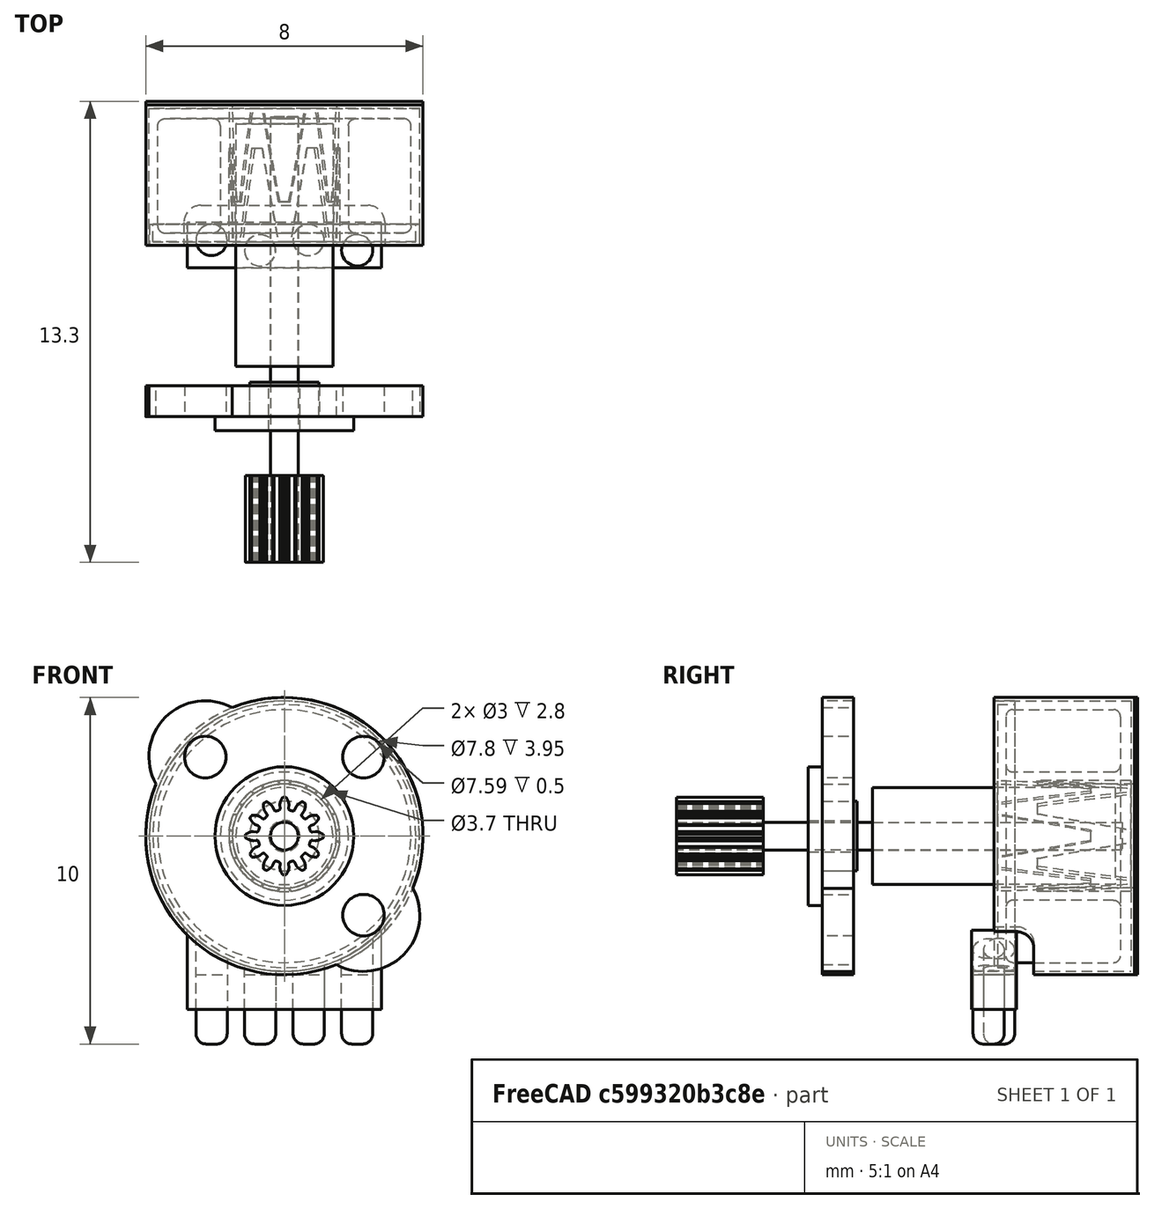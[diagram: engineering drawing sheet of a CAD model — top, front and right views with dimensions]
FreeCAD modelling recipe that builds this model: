
FCSTD DOCUMENT  (FreeCAD 1.0R39109 (Git))
Label: StepperMotor_8mm_i500212644_v4
License: All rights reserved
LicenseURL: https://en.wikipedia.org/wiki/All_rights_reserved
objects: PartDesign::Body×14, PartDesign::SubShapeBinder×13, Sketcher::SketchObject×7, PartDesign::Revolution×6, PartDesign::Plane×5, PartDesign::Pad×5, PartDesign::Pocket×5, PartDesign::FeatureBase×3, PartDesign::PolarPattern×2, PartDesign::Draft×2, App::VarSet×1, Part::Part2DObjectPython×1, PartDesign::Fillet×1, PartDesign::ShapeBinder×1, App::Part×1, App::Link×1, App::FeaturePython×1, Assembly::JointGroup×1, Assembly::AssemblyObject×1
note: 115 computed .brp shape members not serialized (recipe doc carries the construction recipe); baked Part::Feature solids carry a one-line shape summary decoded from their .brp

FEATURE [App::VarSet] VarSet
  Base_CanBodyInnerDiameter = 3
  Base_CanFingerMinorCircumference = 0.25
  Base_FingerClearanceAngle = 13.369
  BodyDiameter = 8
  BushingCollarLength = 1.4
  BushingCollarRadius = 1
  BushingFlangeRadius = 2
  BushingFlangeThickness = 0.4
  BushingMountingPlateClearance = 0.01
  BushingShaftClearance = 0.05
  CanBodyThickness = 0.1
  CanFingerLength = 1.25
  CoilBobbinDepth = 3.5
  CoilBobbinInternalRadius = 1.75
  CoilBobbinOuterRadius = 3.65
  CoilBobbinThickness = 0.1
  ConnectorBodyForwardClearance = 0.5
  ConnectorBodyHeight = 1
  ConnectorBodyLateralClearance = 0.1
  ConnectorBodyThickness = 1.3
  ConnectorBodyWidth = 5.6
  EndCapThickness = 0.1
  FingerClearance = 0.35
  FingerGusset = 0.5
  FingerRootAngle = 46.631
  FingerTeethAngle = 8
  GearHeadDiameter = 2.3
  GearHeadLength = 2.5
  MagnetCanClearance = 0.1
  MagnetLength = 7
  MagnetRadius = 1.4
  MountingHoleDiameter = 1.2
  MountingHolePitch = 6.4519
  MountingPlateThickness = 0.9
  NumFingers = 6
  PinDiameter = 0.9
  PinLength = 1
  PinOffset = 0.15
  PinPitch = 1.4
  PolePlateCanClearance = 0.005
  ShaftEndClearance = 0.45
  ShaftLength = 12.85
  ShaftThickness = 0.8
  TotalLength = 13.3
  expr: Base_CanFingerMinorCircumference = Base_CanBodyInnerDiameter / 2 - CanFingerLength
  expr: Base_FingerClearanceAngle = FingerClearance / (Base_CanBodyInnerDiameter * pi) * 360
  expr: FingerRootAngle = (Base_CanBodyInnerDiameter * pi / NumFingers - FingerClearance) / (Base_CanBodyInnerDiameter * pi) * 360
FEATURE [Sketcher::SketchObject] Sketch  label="MasterSketchFront"
  ArcFitTolerance = 1e-06
  AttachmentSupport = -> [XZ_Plane001]
  FullyConstrained = true
  MakeInternals = false
  MapMode = 5
  Placement = pos=(0,0,0) rot=(1,0,0;1.5708rad)
  expr: .Constraints.ConnectorBodyHeight = VarSet.ConnectorBodyHeight
  expr: Constraints[1] = VarSet.BodyDiameter
  expr: Constraints[27] = VarSet.PinPitch
  expr: Constraints[28] = VarSet.PinLength
  expr: Constraints[30] = VarSet.CanBodyThickness
  expr: Constraints[37] = VarSet.Base_CanBodyInnerDiameter
  expr: Constraints[38] = VarSet.CanFingerLength
  expr: Constraints[41] = VarSet.Base_CanBodyInnerDiameter / 2 - VarSet.CanFingerLength
  expr: Constraints[46] = VarSet.Base_FingerClearanceAngle
  expr: Constraints[47] = VarSet.FingerRootAngle
  expr: Constraints[49] = VarSet.CanBodyThickness * 2 + VarSet.Base_CanBodyInnerDiameter
  expr: Constraints[8] = VarSet.ConnectorBodyWidth
  sketch-geometry (22):
    g0: Circle CenterX=-1e-16 CenterY=0 CenterZ=0 NormalX=0 NormalY=0 NormalZ=1 AngleXU=0 Radius=4
    g1: LineSegment StartX=-2.8 StartY=-2.85657 StartZ=0 EndX=-2.8 EndY=-5 EndZ=0
    g2: LineSegment StartX=-2.8 StartY=-5 StartZ=0 EndX=2.8 EndY=-5 EndZ=0
    g3: LineSegment StartX=2.8 StartY=-5 StartZ=0 EndX=2.8 EndY=-2.85657 EndZ=0
    g4: LineSegment StartX=-2.1 StartY=-5 StartZ=0 EndX=-2.1 EndY=-6 EndZ=0
    g5: LineSegment StartX=-0.7 StartY=-5 StartZ=0 EndX=-0.7 EndY=-6 EndZ=0
    g6: LineSegment StartX=0.7 StartY=-5 StartZ=0 EndX=0.7 EndY=-6 EndZ=0
    g7: LineSegment StartX=2.1 StartY=-5 StartZ=0 EndX=2.1 EndY=-6 EndZ=0
    g8: LineSegment [constr] StartX=-2.1 StartY=-5 StartZ=0 EndX=-0.7 EndY=-5 EndZ=0
    g9: LineSegment [constr] StartX=-0.7 StartY=-5 StartZ=0 EndX=0.7 EndY=-5 EndZ=0
    g10: Circle CenterX=-1e-16 CenterY=0 CenterZ=0 NormalX=0 NormalY=0 NormalZ=1 AngleXU=0 Radius=3.9
    g11: Circle CenterX=-1e-16 CenterY=0 CenterZ=0 NormalX=0 NormalY=0 NormalZ=1 AngleXU=0 Radius=1.5
    g12: ArcOfCircle CenterX=-1e-16 CenterY=0 CenterZ=0 NormalX=0 NormalY=0 NormalZ=1 AngleXU=0 Radius=0.25 StartAngle=1.16386 EndAngle=1.97773
    g13: LineSegment StartX=-0.0989485 StartY=0.229585 StartZ=0 EndX=-0.593691 EndY=1.37751 EndZ=0
    g14: LineSegment StartX=0.0989485 StartY=0.229585 StartZ=0 EndX=0.593691 EndY=1.37751 EndZ=0
    g15: LineSegment StartX=-0.896112 StartY=1.20291 StartZ=0 EndX=-2e-16 EndY=0 EndZ=0
    g16: LineSegment [constr] StartX=-0.593691 StartY=1.37751 StartZ=0 EndX=-1e-16 EndY=0 EndZ=0
    g17: Circle CenterX=-1e-16 CenterY=0 CenterZ=0 NormalX=0 NormalY=0 NormalZ=1 AngleXU=0 Radius=1.6
    g18: LineSegment StartX=-0.896112 StartY=1.20291 StartZ=0 EndX=-0.955853 EndY=1.2831 EndZ=0
    g19: LineSegment StartX=-0.593691 StartY=1.37751 StartZ=0 EndX=-0.63327 EndY=1.46934 EndZ=0
    g20: LineSegment StartX=0.593691 StartY=1.37751 StartZ=0 EndX=0.63327 EndY=1.46934 EndZ=0
    g21: GeomPoint X=0 Y=-5 Z=0
  constraints (60):
    c: Coincident(g0,g-1)
    c: Diameter(g0) = 8
    c: Coincident(g1,g2)
    c: Coincident(g2,g3)
    c: Vertical(g1)
    c: Vertical(g3)
    c: PointOnObject(g1,g0)
    c: PointOnObject(g3,g0)
    c: DistanceX(g2,g2) = 5.6
    c: Symmetric(g2,g1,g-2)
    c: Distance(g0,g2) = 1  'ConnectorBodyHeight'
    c: PointOnObject(g4,g2)
    c: Vertical(g4)
    c: PointOnObject(g5,g2)
    c: Vertical(g5)
    c: Vertical(g6)
    c: Vertical(g7)
    c: Equal(g7,g6)
    c: Equal(g6,g5)
    c: Equal(g5,g4)
    c: Symmetric(g7,g4,g-2)
    c: Symmetric(g5,g6,g-2)
    c: Coincident(g8,g4)
    c: Coincident(g8,g5)
    c: Coincident(g9,g5)
    c: Coincident(g9,g6)
    c: Equal(g8,g9)
    c: Distance(g5,g4) = 1.4
    c: DistanceY(g4,g4) = 1
    c: Coincident(g10,g0)
    c: Distance(g10,g0) = 0.1
    c: Coincident(g11,g0)
    c: Coincident(g12,g0)
    c: PointOnObject(g13,g11)
    c: PointOnObject(g14,g11)
    c: Horizontal(g14,g13)
    c: Horizontal(g14,g13)
    c: Diameter(g11) = 3
    c: Distance(g14,g14) = 1.25
    c: Coincident(g12,g13)
    c: Coincident(g12,g14)
    c: Radius(g12) = 0.25
    c: PointOnObject(g15,g11)
    c: Coincident(g15,g0)
    c: Coincident(g16,g13)
    c: Coincident(g16,g0)
    c: Angle(g13,g15) = 0.233333
    c: Angle(g14,g13) = 0.813864
    c: Coincident(g17,g0)
    c: Diameter(g17) = 3.2
    c: Coincident(g18,g15)
    c: PointOnObject(g18,g17)
    c: Coincident(g19,g13)
    c: PointOnObject(g19,g17)
    c: Perpendicular(g11,g19)
    c: Perpendicular(g11,g18)
    c: Coincident(g20,g14)
    c: PointOnObject(g20,g17)
    c: Perpendicular(g11,g20)
    c: Symmetric(g2,g2,g21)
FEATURE [Sketcher::SketchObject] Sketch001  label="MasterSketchRight"
  ArcFitTolerance = 1e-06
  AttachmentSupport = -> [YZ_Plane001]
  ExternalGeometry = -> [Sketch]
  FullyConstrained = false
  MakeInternals = false
  MapMode = 5
  Placement = pos=(0,0,0) rot=(0.57735,0.57735,0.57735;2.0944rad)
  expr: .Constraints.BushingFlangeRadius = VarSet.BushingFlangeRadius
  expr: .Constraints.BushingShaftClearance = VarSet.BushingShaftClearance
  expr: .Constraints.EndCapThickness = VarSet.EndCapThickness
  expr: .Constraints.ShaftThickness = VarSet.ShaftThickness
  expr: Constraints[116] = VarSet.PolePlateCanClearance
  expr: Constraints[161] = VarSet.CoilBobbinThickness
  expr: Constraints[162] = VarSet.CoilBobbinInternalRadius
  expr: Constraints[163] = VarSet.CoilBobbinDepth
  expr: Constraints[164] = VarSet.CoilBobbinOuterRadius
  expr: Constraints[194] = VarSet.Base_CanBodyInnerDiameter / 2
  expr: Constraints[195] = VarSet.CanFingerLength
  expr: Constraints[59] = VarSet.BushingCollarRadius
  expr: Constraints[60] = VarSet.BushingMountingPlateClearance
  expr: Constraints[61] = VarSet.BushingFlangeThickness
  expr: Constraints[63] = VarSet.BushingCollarLength
  expr: Constraints[65] = VarSet.GearHeadDiameter
  expr: Constraints[66] = VarSet.GearHeadLength
  expr: Constraints[67] = VarSet.MountingPlateThickness
  expr: Constraints[71] = VarSet.TotalLength
  expr: Constraints[72] = VarSet.ShaftLength
  expr: Constraints[92] = VarSet.MagnetRadius
  expr: Constraints[93] = VarSet.MagnetLength
  sketch-geometry (80):
    g0: LineSegment StartX=0 StartY=0 StartZ=0 EndX=3.7 EndY=0 EndZ=0
    g1: LineSegment StartX=0 StartY=0 StartZ=0 EndX=-9.15 EndY=0 EndZ=0
    g2: GeomPoint X=-6.65 Y=0 Z=0
    g3: GeomPoint X=-5.35 Y=0 Z=0
    g4: GeomPoint X=-4.05 Y=0 Z=0
    g5: GeomPoint X=-4.95 Y=0 Z=0
    g6: GeomPoint X=3.7 Y=0 Z=0
    g7: LineSegment StartX=-9.15 StartY=1.15 StartZ=0 EndX=-9.15 EndY=-1.15 EndZ=0
    g8: LineSegment StartX=-9.15 StartY=-1.15 StartZ=0 EndX=-6.65 EndY=-1.15 EndZ=0
    g9: LineSegment StartX=-6.65 StartY=-1.15 StartZ=0 EndX=-6.65 EndY=1.15 EndZ=0
    g10: LineSegment StartX=-6.65 StartY=1.15 StartZ=0 EndX=-9.15 EndY=1.15 EndZ=0
    g11: LineSegment StartX=-9.15 StartY=0.4 StartZ=0 EndX=-9.15 EndY=-0.4 EndZ=0
    g12: LineSegment StartX=-9.15 StartY=-0.4 StartZ=0 EndX=3.7 EndY=-0.4 EndZ=0
    g13: LineSegment StartX=3.7 StartY=-0.4 StartZ=0 EndX=3.7 EndY=0.4 EndZ=0
    g14: LineSegment StartX=3.7 StartY=0.4 StartZ=0 EndX=0 EndY=0.4 EndZ=0
    g15: LineSegment StartX=-5.35 StartY=2 StartZ=0 EndX=-5.35 EndY=0.45 EndZ=0
    g16: LineSegment StartX=-5.35 StartY=0.45 StartZ=0 EndX=-3.95 EndY=0.45 EndZ=0
    g17: LineSegment StartX=-3.95 StartY=0.45 StartZ=0 EndX=-3.95 EndY=1 EndZ=0
    g18: LineSegment StartX=-4.95 StartY=1 StartZ=0 EndX=-4.95 EndY=2 EndZ=0
    g19: LineSegment StartX=-4.95 StartY=2 StartZ=0 EndX=-5.35 EndY=2 EndZ=0
    g20: LineSegment StartX=-4.95 StartY=4 StartZ=0 EndX=-4.95 EndY=1.01 EndZ=0
    g21: LineSegment StartX=-4.95 StartY=1.01 StartZ=0 EndX=-4.05 EndY=1.01 EndZ=0
    g22: LineSegment StartX=-4.05 StartY=4 StartZ=0 EndX=-4.95 EndY=4 EndZ=0
    g23: LineSegment StartX=4.15 StartY=4 StartZ=0 EndX=4.15 EndY=0 EndZ=0
    g24: LineSegment StartX=4.05 StartY=0 StartZ=0 EndX=4.05 EndY=4 EndZ=0
    g25: LineSegment StartX=4.05 StartY=4 StartZ=0 EndX=4.15 EndY=4 EndZ=0
    g26: LineSegment StartX=-4.05 StartY=4 StartZ=0 EndX=9e-16 EndY=4 EndZ=0
    g27: LineSegment StartX=9e-16 StartY=4 StartZ=0 EndX=4.05 EndY=4 EndZ=0
    g28: LineSegment StartX=-4.95 StartY=1 StartZ=0 EndX=-3.95 EndY=1 EndZ=0
    g29: GeomPoint X=4.05 Y=0 Z=0
    g30: LineSegment StartX=-3.95 StartY=3.9 StartZ=0 EndX=-3.95 EndY=1.6 EndZ=0
    g31: LineSegment StartX=9e-16 StartY=3.9 StartZ=0 EndX=-3.95 EndY=3.9 EndZ=0
    g32: LineSegment StartX=-3.5 StartY=0.4 StartZ=0 EndX=3.5 EndY=0.4 EndZ=0
    g33: LineSegment StartX=3.5 StartY=0.4 StartZ=0 EndX=3.5 EndY=1.4 EndZ=0
    g34: LineSegment StartX=3.5 StartY=1.4 StartZ=0 EndX=-3.5 EndY=1.4 EndZ=0
    g35: LineSegment StartX=-3.5 StartY=1.4 StartZ=0 EndX=-3.5 EndY=0.4 EndZ=0
    g36: LineSegment [constr] StartX=9e-16 StartY=3.9 StartZ=0 EndX=9e-16 EndY=4 EndZ=0
    g37: LineSegment [constr] StartX=-3.95 StartY=3.9 StartZ=0 EndX=-4.05 EndY=3.9 EndZ=0
    g38: GeomPoint X=0 Y=1.4 Z=0
    g39: LineSegment StartX=-0.6 StartY=3.895 StartZ=0 EndX=9e-16 EndY=3.895 EndZ=0
    g40: LineSegment StartX=9e-16 StartY=3.895 StartZ=0 EndX=4e-16 EndY=1.5 EndZ=0
    g41: LineSegment StartX=-0.1 StartY=1.6 StartZ=0 EndX=-0.1 EndY=3.795 EndZ=0
    g42: LineSegment StartX=-0.1 StartY=3.795 StartZ=0 EndX=-0.6 EndY=3.795 EndZ=0
    g43: LineSegment StartX=-0.6 StartY=3.795 StartZ=0 EndX=-0.6 EndY=3.895 EndZ=0
    g44: LineSegment [constr] StartX=-0.1 StartY=3.795 StartZ=0 EndX=8e-16 EndY=3.795 EndZ=0
    g45: LineSegment StartX=-1.25 StartY=1.6 StartZ=0 EndX=-1.25 EndY=1.5 EndZ=0
    g46: LineSegment StartX=-3.95 StartY=1.6 StartZ=0 EndX=-1.25 EndY=1.6 EndZ=0
    g47: LineSegment StartX=-0.1 StartY=1.6 StartZ=0 EndX=-2.8 EndY=1.6 EndZ=0
    g48: LineSegment StartX=9e-16 StartY=3.895 StartZ=0 EndX=4e-16 EndY=1.5 EndZ=0
    g49: LineSegment StartX=-3.65 StartY=3.45 StartZ=0 EndX=-3.65 EndY=2.05 EndZ=0
    g50: LineSegment StartX=-3.45 StartY=1.85 StartZ=0 EndX=-0.55 EndY=1.85 EndZ=0
    g51: LineSegment StartX=-0.35 StartY=2.05 StartZ=0 EndX=-0.35 EndY=3.45 EndZ=0
    g52: LineSegment StartX=-0.55 StartY=3.65 StartZ=0 EndX=-3.45 EndY=3.65 EndZ=0
    g53: ArcOfCircle CenterX=-3.45 CenterY=3.45 CenterZ=0 NormalX=0 NormalY=0 NormalZ=1 AngleXU=0 Radius=0.2 StartAngle=1.5708 EndAngle=3.14159
    g54: ArcOfCircle CenterX=-3.45 CenterY=2.05 CenterZ=0 NormalX=0 NormalY=0 NormalZ=1 AngleXU=0 Radius=0.2 StartAngle=3.14159 EndAngle=4.71239
    g55: ArcOfCircle CenterX=-0.55 CenterY=2.05 CenterZ=0 NormalX=0 NormalY=0 NormalZ=1 AngleXU=0 Radius=0.2 StartAngle=4.71239 EndAngle=6.28319
    g56: ArcOfCircle CenterX=-0.55 CenterY=3.45 CenterZ=0 NormalX=0 NormalY=0 NormalZ=1 AngleXU=0 Radius=0.2 StartAngle=3e-16 EndAngle=1.5708
    g57: GeomPoint [constr] X=-3.65 Y=3.65 Z=0
    g58: GeomPoint [constr] X=-0.35 Y=1.85 Z=0
    g59: LineSegment StartX=-3.75 StartY=3.65 StartZ=0 EndX=-3.65 EndY=3.65 EndZ=0
    g60: LineSegment StartX=-3.65 StartY=3.65 StartZ=0 EndX=-3.65 EndY=1.85 EndZ=0
    g61: LineSegment StartX=-3.65 StartY=1.85 StartZ=0 EndX=-0.35 EndY=1.85 EndZ=0
    g62: LineSegment StartX=-0.35 StartY=1.85 StartZ=0 EndX=-0.35 EndY=3.65 EndZ=0
    g63: LineSegment StartX=-0.35 StartY=3.65 StartZ=0 EndX=-0.25 EndY=3.65 EndZ=0
    g64: LineSegment StartX=-0.25 StartY=3.65 StartZ=0 EndX=-0.25 EndY=1.75 EndZ=0
    g65: LineSegment StartX=-0.25 StartY=1.75 StartZ=0 EndX=-3.75 EndY=1.75 EndZ=0
    g66: LineSegment StartX=-3.75 StartY=1.75 StartZ=0 EndX=-3.75 EndY=3.65 EndZ=0
    g67: LineSegment [constr] StartX=-0.35 StartY=1.85 StartZ=0 EndX=-0.35 EndY=1.75 EndZ=0
    g68: LineSegment [constr] StartX=9e-16 StartY=3.9 StartZ=0 EndX=9e-16 EndY=4 EndZ=0
    g69: LineSegment StartX=9e-16 StartY=4 StartZ=0 EndX=9e-16 EndY=3.9 EndZ=0
    g70: LineSegment StartX=-4.05 StartY=1.01 StartZ=0 EndX=-4.05 EndY=1.5 EndZ=0
    g71: LineSegment StartX=-4.05 StartY=1.5 StartZ=0 EndX=-4.05 EndY=3.9 EndZ=0
    g72: LineSegment StartX=-4.05 StartY=3.9 StartZ=0 EndX=-4.05 EndY=4 EndZ=0
    g73: LineSegment StartX=-1.25 StartY=1.6 StartZ=0 EndX=-2.8 EndY=1.6 EndZ=0
    g74: LineSegment StartX=-4.05 StartY=1.5 StartZ=0 EndX=-1.25 EndY=1.5 EndZ=0
    g75: LineSegment StartX=-1.25 StartY=1.5 StartZ=0 EndX=-2.8 EndY=1.5 EndZ=0
    g76: LineSegment StartX=-2.8 StartY=1.6 StartZ=0 EndX=-2.8 EndY=1.5 EndZ=0
    g77: LineSegment StartX=-2.8 StartY=1.5 StartZ=0 EndX=4e-16 EndY=1.5 EndZ=0
    g78: LineSegment StartX=4.05 StartY=0 StartZ=0 EndX=4.15 EndY=0 EndZ=0
    g79: LineSegment StartX=-3.5 StartY=0.4 StartZ=0 EndX=-9.15 EndY=0.4 EndZ=0
  constraints (205):
    c: Coincident(g0,g-1)
    c: PointOnObject(g78,g-1)
    c: Coincident(g1,g0)
    c: PointOnObject(g1,g-1)
    c: PointOnObject(g2,g1)
    c: PointOnObject(g4,g1)
    c: PointOnObject(g5,g1)
    c: PointOnObject(g6,g0)
    c: Coincident(g7,g8)
    c: Coincident(g8,g9)
    c: Coincident(g9,g10)
    c: Coincident(g10,g7)
    c: Vertical(g7)
    c: Vertical(g9)
    c: Horizontal(g8)
    c: Symmetric(g7,g7,g1)
    c: Symmetric(g8,g9,g2)
    c: Coincident(g11,g12)
    c: Coincident(g12,g13)
    c: Coincident(g13,g14)
    c: Coincident(g79,g11)
    c: Vertical(g11)
    c: Vertical(g13)
    c: Horizontal(g12)
    c: Symmetric(g12,g13,g6)
    c: Vertical(g15)
    c: Coincident(g15,g16)
    c: Horizontal(g16)
    c: Coincident(g16,g17)
    c: Vertical(g18)
    c: Coincident(g18,g19)
    c: Coincident(g19,g15)
    c: Horizontal(g19)
    c: Vertical(g17)
    c: Vertical(g3,g15)
    c: Coincident(g20,g21)
    c: Coincident(g22,g20)
    c: Horizontal(g21)
    c: Horizontal(g22)
    c: Vertical(g20,g5)
    c: Vertical(g21,g4)
    c: Distance(g12,g14) = 0.8  'ShaftThickness'
    c: Distance(g15,g14) = 0.05  'BushingShaftClearance'
    c: DistanceY(g3,g15) = 2  'BushingFlangeRadius'
    c: Coincident(g24,g25)
    c: Coincident(g25,g23)
    c: Vertical(g23)
    c: Vertical(g24)
    c: Horizontal(g25)
    c: Distance(g23,g24) = 0.1  'EndCapThickness'
    c: Coincident(g26,g-3)
    c: Horizontal(g26)
    c: Coincident(g27,g26)
    c: Coincident(g27,g24)
    c: Symmetric(g24,g22,g26)
    c: DistanceX(g20,g23) = 9.1  'MeasuredBodyLength'
    c: Coincident(g28,g18)
    c: Coincident(g28,g17)
    c: Horizontal(g28)
    c: DistanceY(g4,g17) = 1
    c: Distance(g21,g28) = 0.01
    c: Distance(g19,g19) = 0.4
    c: Tangent(g18,g20)
    c: DistanceX(g15,g16) = 1.4
    c: Symmetric(g11,g11,g1)
    c: DistanceY(g7,g7) = 2.3
    c: DistanceX(g10,g10) = 2.5
    c: DistanceX(g22,g22) = 0.9
    c: PointOnObject(g3,g1)
    c: PointOnObject(g29,g78)
    c: PointOnObject(g29,g24)
    c: DistanceX(g1,g78) = 13.3
    c: DistanceX(g1,g6) = 12.85
    c: DistanceX(g13,g29) = 0.35  'ShafteendClearance'
    c: Coincident(g31,g30)
    c: Vertical(g30)
    c: Horizontal(g31)
    c: Coincident(g32,g33)
    c: Coincident(g33,g34)
    c: Coincident(g34,g35)
    c: Coincident(g35,g32)
    c: Horizontal(g32)
    c: Horizontal(g34)
    c: Vertical(g33)
    c: Vertical(g35)
    c: PointOnObject(g32,g79)
    c: Coincident(g36,g31)
    c: Coincident(g36,g26)
    c: Coincident(g37,g30)
    c: Horizontal(g37)
    c: Equal(g37,g36)
    c: Coincident(g31,g-4)
    c: Distance(g0,g34) = 1.4
    c: Distance(g33,g35) = 7
    c: Symmetric(g34,g34,g38)
    c: Vertical(g38,g0)
    c: PointOnObject(g39,g-4)
    c: Horizontal(g39)
    c: Coincident(g39,g40)
    c: PointOnObject(g40,g-4)
    c: Vertical(g41)
    c: Coincident(g41,g42)
    c: Horizontal(g42)
    c: Coincident(g42,g43)
    c: Coincident(g43,g39)
    c: Vertical(g43)
    c: Coincident(g44,g41)
    c: PointOnObject(g44,g40)
    c: Horizontal(g44)
    c: Equal(g44,g43)
    c: Vertical(g45)
    c: Coincident(g46,g30)
    c: Coincident(g46,g45)
    c: Horizontal(g46)
    c: Coincident(g47,g41)
    c: Horizontal(g47)
    c: Distance(g31,g39) = 0.005
    c: DistanceX(g42,g42) = 0.5  'PolePlateFlangeLength'
    c: Equal(g47,g46)
    c: Coincident(g48,g39)
    c: Coincident(g48,g40)
    c: Tangent(g49,g53) = -1.5708
    c: Tangent(g49,g54) = -1.5708
    c: Tangent(g50,g54) = -1.5708
    c: Tangent(g50,g55) = -1.5708
    c: Tangent(g51,g55) = -1.5708
    c: Tangent(g51,g56) = -1.5708
    c: Tangent(g52,g56) = -1.5708
    c: Tangent(g52,g53) = -1.5708
    c: Vertical(g49)
    c: Vertical(g51)
    c: Horizontal(g50)
    c: Horizontal(g52)
    c: Equal(g53,g54)
    c: Equal(g54,g55)
    c: Equal(g55,g56)
    c: PointOnObject(g57,g49)
    c: PointOnObject(g57,g52)
    c: PointOnObject(g58,g50)
    c: PointOnObject(g58,g51)
    c: Coincident(g59,g60)
    c: Coincident(g60,g61)
    c: Coincident(g61,g62)
    c: Coincident(g62,g63)
    c: Coincident(g63,g64)
    c: Vertical(g64)
    c: Coincident(g64,g65)
    c: Horizontal(g65)
    c: Coincident(g65,g66)
    c: Coincident(g66,g59)
    c: Vertical(g66)
    c: Equal(g59,g63)
    c: Tangent(g49,g60)
    c: Tangent(g51,g62)
    c: Tangent(g63,g59)
    c: Tangent(g59,g52)
    c: Tangent(g50,g61)
    c: Coincident(g67,g58)
    c: PointOnObject(g67,g65)
    c: Vertical(g67)
    c: Equal(g67,g63)
    c: Distance(g49,g66) = 0.1
    c: DistanceY(g0,g64) = 1.75
    c: DistanceX(g65,g64) = 3.5
    c: DistanceY(g0,g63) = 3.65
    c: Coincident(g68,g31)
    c: Coincident(g68,g26)
    c: Coincident(g69,g26)
    c: Coincident(g69,g31)
    c: Coincident(g70,g21)
    c: Vertical(g70)
    c: Coincident(g71,g37)
    c: Vertical(g71)
    c: Coincident(g72,g37)
    c: Coincident(g72,g22)
    c: Coincident(g26,g22)
    c: Coincident(g73,g45)
    c: Coincident(g73,g47)
    c: Horizontal(g73)
    c: Coincident(g74,g70)
    c: Coincident(g74,g45)
    c: Horizontal(g74)
    c: Coincident(g75,g45)
    c: Horizontal(g75)
    c: Coincident(g76,g47)
    c: Coincident(g76,g75)
    c: Coincident(g77,g75)
    c: Coincident(g77,g40)
    c: Horizontal(g77)
    c: Vertical(g76)
    c: Coincident(g71,g70)
    c: Vertical(g72)
    c: Equal(g45,g37)
    c: Equal(g44,g37)
    c: Distance(g40,g0) = 1.5
    c: DistanceX(g45,g40) = 1.25
    c: PointOnObject(g24,g78)
    c: Coincident(g78,g23)
    c: PointOnObject(g0,g13)
    c: PointOnObject(g78,g24)
    c: Distance(g41,g64) = 0.15  'BobbinOffset'
    c: Radius(g53) = 0.2  'CoilRoundness'
    c: Horizontal(g0)
    c: Horizontal(g78)
    c: PointOnObject(g14,g-4)
FEATURE [PartDesign::Plane] DatumPlane  label="GearHeadDatum"
  AttachmentSupport = -> [Sketch001,XZ_Plane001]
  Length = 10
  MapMode = 6
  Placement = pos=(0,-9.15,0) rot=(0.57735,-0.57735,0.57735;2.0944rad)
  ResizeMode = 1
  Width = 10
FEATURE [PartDesign::Plane] DatumPlane001  label="BushingFlangeDatum"
  AttachmentSupport = -> [Sketch001,XZ_Plane001]
  Length = 10
  MapMode = 6
  Placement = pos=(0,-5.35,0) rot=(0.57735,-0.57735,0.57735;2.0944rad)
  ResizeMode = 1
  Width = 10
FEATURE [PartDesign::Plane] DatumPlane002  label="MountingPlateDatum"
  AttachmentSupport = -> [Sketch001,XZ_Plane001]
  Length = 10
  MapMode = 6
  Placement = pos=(0,-4.95,0) rot=(0.57735,-0.57735,0.57735;2.0944rad)
  ResizeMode = 1
  Width = 10
FEATURE [PartDesign::Plane] DatumPlane003  label="EndCapDatum"
  AttachmentSupport = -> [Sketch001,XZ_Plane001]
  Length = 10
  MapMode = 6
  Placement = pos=(0,4.05,0) rot=(0.57735,-0.57735,0.57735;2.0944rad)
  ResizeMode = 1
  Width = 10
FEATURE [Sketcher::SketchObject] Sketch002
  ArcFitTolerance = 1e-06
  AttachmentSupport = -> [DatumPlane]
  FullyConstrained = true
  MakeInternals = false
  MapMode = 5
  Placement = pos=(0,-9.15,0) rot=(0.57735,-0.57735,0.57735;2.0944rad)
  expr: Constraints[1] = VarSet.ShaftThickness
  sketch-geometry (1):
    g0: Circle CenterX=0 CenterY=0 CenterZ=0 NormalX=0 NormalY=0 NormalZ=1 AngleXU=0 Radius=0.4
  constraints (2):
    c: Coincident(g0,g-1)
    c: Diameter(g0) = 0.8
FEATURE [PartDesign::Pad] Pad
  Direction = (0,-1,0)
  Length = 12.85
  Length2 = 10
  Placement = pos=(0,-9.15,0) rot=(0.57735,-0.57735,0.57735;2.0944rad)
  Profile = -> Sketch002
  ReferenceAxis = -> Sketch002 [N_Axis]
  Refine = true
  Reversed = true
  Suppressed = false
  Type = 0
  expr: Length = VarSet.ShaftLength
FEATURE [PartDesign::Body] Body  label="Shaft"
  AllowCompound = false
  Group = -> [Sketch002,Pad]
  Origin = -> Origin
  Tip = -> Pad
FEATURE [Sketcher::SketchObject] Sketch004  label="MountingPlateMasterSketch"
  ArcFitTolerance = 1e-06
  AttachmentSupport = -> [DatumPlane002]
  ExternalGeometry = -> [Sketch,Sketch001]
  FullyConstrained = false
  MakeInternals = false
  MapMode = 5
  Placement = pos=(0,-4.95,0) rot=(0.57735,-0.57735,0.57735;2.0944rad)
  expr: Constraints[14] = VarSet.MountingHoleDiameter
  expr: Constraints[17] = VarSet.MountingHolePitch
  sketch-geometry (14):
    g0: ArcOfCircle CenterX=0 CenterY=0 CenterZ=0 NormalX=0 NormalY=0 NormalZ=1 AngleXU=0 Radius=4 StartAngle=1.18551 EndAngle=3.52688
    g1: LineSegment [constr] StartX=5.10029 StartY=5.10029 StartZ=0 EndX=-5.10029 EndY=-5.10029 EndZ=0
    g2: Circle CenterX=2.28109 CenterY=2.28109 CenterZ=0 NormalX=0 NormalY=0 NormalZ=1 AngleXU=0 Radius=0.6
    g3: Circle CenterX=-2.28109 CenterY=-2.28109 CenterZ=0 NormalX=0 NormalY=0 NormalZ=1 AngleXU=0 Radius=0.6
    g4: ArcOfCircle CenterX=-2.28109 CenterY=-2.28109 CenterZ=0 NormalX=0 NormalY=0 NormalZ=1 AngleXU=0 Radius=1.62405 StartAngle=2.64216 EndAngle=5.21182
    g5: ArcOfCircle CenterX=2.28109 CenterY=2.28109 CenterZ=0 NormalX=0 NormalY=0 NormalZ=1 AngleXU=0 Radius=1.62405 StartAngle=5.78375 EndAngle=8.35342
    g6: ArcOfCircle CenterX=0 CenterY=0 CenterZ=0 NormalX=0 NormalY=0 NormalZ=1 AngleXU=0 Radius=4 StartAngle=4.32711 EndAngle=6.66847
    g7: Circle [constr] CenterX=0 CenterY=0 CenterZ=0 NormalX=0 NormalY=0 NormalZ=1 AngleXU=0 Radius=3.22595
    g8: Circle CenterX=2.28109 CenterY=-2.28109 CenterZ=0 NormalX=0 NormalY=0 NormalZ=1 AngleXU=0 Radius=0.6
    g9: GeomPoint X=3.42947 Y=3.42947 Z=0
    g10: GeomPoint X=-3.42947 Y=-3.42947 Z=0
    g11: ArcOfCircle CenterX=0 CenterY=0 CenterZ=0 NormalX=0 NormalY=0 NormalZ=1 AngleXU=0 Radius=4 StartAngle=1.18551 EndAngle=3.52688
    g12: ArcOfCircle CenterX=0 CenterY=0 CenterZ=0 NormalX=0 NormalY=0 NormalZ=1 AngleXU=0 Radius=4 StartAngle=4.32711 EndAngle=6.66847
    g13: Circle CenterX=0 CenterY=0 CenterZ=0 NormalX=0 NormalY=0 NormalZ=1 AngleXU=0 Radius=1.01
  constraints (38):
    c: Coincident(g0,g-1)
    c: Symmetric(g1,g1,g0)
    c: Angle(g1,g-2) = 0.785398
    c: PointOnObject(g2,g1)
    c: Equal(g3,g2)
    c: Symmetric(g3,g2,g0)
    c: Equal(g5,g4)
    c: Symmetric(g4,g5,g0)
    c: Coincident(g0,g5)
    c: Coincident(g6,g5)
    c: Equal(g0,g6)
    c: Coincident(g0,g6)
    c: Coincident(g4,g6)
    c: Coincident(g4,g0)
    c: Diameter(g2) = 1.2
    c: Coincident(g5,g2)
    c: PointOnObject(g5,g-3)
    c: Distance(g2,g3) = 6.4519
    c: Radius(g5) = 1.62405
    c: Coincident(g7,g0)
    c: PointOnObject(g2,g7)
    c: PointOnObject(g8,g7)
    c: Equal(g8,g3)
    c: Horizontal(g8,g3)
    c: PointOnObject(g9,g5)
    c: PointOnObject(g10,g1)
    c: PointOnObject(g9,g1)
    c: PointOnObject(g10,g4)
    c: Distance(g9,g10) = 9.7  'MountingTabWidth'
    c: Coincident(g11,g0)
    c: Coincident(g11,g5)
    c: PointOnObject(g12,g5)
    c: Equal(g11,g12)
    c: PointOnObject(g11,g4)
    c: PointOnObject(g12,g4)
    c: Coincident(g11,g12)
    c: Coincident(g13,g0)
    c: PointOnObject(g-5,g13)
FEATURE [PartDesign::SubShapeBinder] Binder006
  BindCopyOnChange = 0
  BindMode = 0
  ClaimChildren = false
  Context = -> Part [Body004.Binder006.]
  Fuse = false
  MakeFace = true
  OffsetFill = false
  OffsetIntersection = false
  OffsetJoinType = 0
  OffsetOpenResult = false
  PartialLoad = false
  Refine = true
  Relative = true
  Support = -> [Sketch[Edge11,Edge13,Edge12,Edge10,Edge17,Edge19,Edge18,Edge16]]
  _Version = 2
FEATURE [PartDesign::SubShapeBinder] Binder
  BindCopyOnChange = 0
  BindMode = 0
  ClaimChildren = false
  Context = -> Part [Body002.Binder.]
  Fuse = false
  MakeFace = true
  OffsetFill = false
  OffsetIntersection = false
  OffsetJoinType = 0
  OffsetOpenResult = false
  PartialLoad = false
  Refine = true
  Relative = true
  Support = -> [Sketch001[Edge17,Edge18,Edge19,Edge20,Edge21,Edge16]]
  _Version = 2
FEATURE [PartDesign::Revolution] Revolution
  Angle = 360
  Angle2 = 60
  Axis = (1e-16,1,-1e-16)
  Base = (0,0,0)
  Profile = -> Binder
  ReferenceAxis = -> Y_Axis003
  Refine = true
  Reversed = true
  Suppressed = false
  Type = 0
FEATURE [PartDesign::Body] Body002  label="Bushing"
  AllowCompound = false
  Group = -> [Revolution,Binder]
  Origin = -> Origin003
  Tip = -> Revolution
FEATURE [PartDesign::SubShapeBinder] Binder007
  BindCopyOnChange = 0
  BindMode = 0
  ClaimChildren = false
  Context = -> Part [Body004.Binder007.]
  Fuse = false
  MakeFace = true
  OffsetFill = false
  OffsetIntersection = false
  OffsetJoinType = 0
  OffsetOpenResult = false
  PartialLoad = false
  Refine = true
  Relative = true
  Support = -> [Sketch001[Edge37,Edge26,Edge48,Edge25,Edge49,Edge36,Edge27,Edge28]]
  _Version = 2
FEATURE [PartDesign::Revolution] Revolution001
  Angle = 360
  Angle2 = 60
  Axis = (1e-16,1,-1e-16)
  Base = (0,0,0)
  Profile = -> Binder007
  ReferenceAxis = -> Y_Axis005
  Refine = true
  Reversed = true
  Suppressed = false
  Type = 0
FEATURE [Sketcher::SketchObject] Sketch005
  ArcFitTolerance = 1e-06
  AttachmentSupport = -> [Revolution001]
  ExternalGeometry = -> [Binder006]
  FullyConstrained = true
  MakeInternals = false
  MapMode = 5
  Placement = pos=(-1e-16,-1.25,1e-16) rot=(0,0.707107,0.707107;3.14159rad)
  sketch-geometry (4):
    g0: LineSegment StartX=0.63327 StartY=1.46934 StartZ=0 EndX=0.593691 EndY=1.37751 EndZ=0
    g1: LineSegment StartX=0.955853 StartY=1.2831 StartZ=0 EndX=0.896112 EndY=1.20291 EndZ=0
    g2: ArcOfCircle CenterX=0 CenterY=0 CenterZ=0 NormalX=0 NormalY=0 NormalZ=1 AngleXU=0 Radius=1.5 StartAngle=0.930531 EndAngle=1.16386
    g3: ArcOfCircle CenterX=0 CenterY=0 CenterZ=0 NormalX=0 NormalY=0 NormalZ=1 AngleXU=0 Radius=1.6 StartAngle=0.930531 EndAngle=1.16386
  constraints (10):
    c: Coincident(g0,g-6)
    c: Coincident(g1,g-7)
    c: Coincident(g1,g-7)
    c: Coincident(g3,g2)
    c: Coincident(g3,g-6)
    c: PointOnObject(g3,g1)
    c: Coincident(g2,g0)
    c: Coincident(g2,g1)
    c: Coincident(g2,g-1)
    c: Perpendicular(g2,g0)
FEATURE [PartDesign::Pocket] Pocket
  BaseFeature = -> Revolution001
  Direction = (0,-1,2e-16)
  Length = 0
  Length2 = 5
  Profile = -> Sketch005
  ReferenceAxis = -> Sketch005 [N_Axis]
  Refine = true
  Suppressed = false
  Type = 3
  UpToFace = -> Revolution001 [Face4]
FEATURE [PartDesign::PolarPattern] PolarPattern
  Angle = 360
  Axis = -> Sketch005 [N_Axis]
  BaseFeature = -> Pocket
  Mode = 0
  Occurrences = 6
  Offset = 120
  Originals = -> [Pocket]
  Refine = true
  Suppressed = false
  TransformMode = 0
  expr: Occurrences = VarSet.NumFingers
FEATURE [PartDesign::Draft] Draft
  Angle = 10
  Base = -> PolarPattern [Face22,Face20,Face23,Face7,Face8,Face10,Face13,Face16,Face17,Face14,Face11,Face19]
  BaseFeature = -> PolarPattern
  NeutralPlane = -> PolarPattern [Face30]
  Refine = true
  SupportTransform = false
  Suppressed = false
FEATURE [PartDesign::SubShapeBinder] Binder008
  BindCopyOnChange = 0
  BindMode = 0
  ClaimChildren = false
  Context = -> Part [Body006.Binder008.]
  Fuse = false
  MakeFace = true
  OffsetFill = false
  OffsetIntersection = false
  OffsetJoinType = 0
  OffsetOpenResult = false
  PartialLoad = false
  Refine = true
  Relative = true
  Support = -> [Sketch001[Edge45,Edge44,Edge46,Edge43]]
  _Version = 2
FEATURE [PartDesign::Revolution] Revolution002
  Angle = 360
  Angle2 = 60
  Axis = (1e-16,1,-1e-16)
  Base = (0,0,0)
  Profile = -> Binder008
  ReferenceAxis = -> Y_Axis007
  Refine = true
  Suppressed = false
  Type = 0
FEATURE [PartDesign::Body] Body006  label="EndCap"
  AllowCompound = false
  Group = -> [Binder008,Revolution002]
  Origin = -> Origin007
  Tip = -> Revolution002
FEATURE [PartDesign::SubShapeBinder] Binder009
  BindCopyOnChange = 0
  BindMode = 0
  ClaimChildren = false
  Context = -> Part [Body003.Binder009.]
  Fuse = false
  MakeFace = true
  OffsetFill = false
  OffsetIntersection = false
  OffsetJoinType = 0
  OffsetOpenResult = false
  PartialLoad = false
  Refine = true
  Relative = true
  Support = -> [Sketch004[Edge1,Edge2,Edge3,Edge4,Vertex5,Edge10,Edge9,Edge8]]
  _Version = 2
FEATURE [PartDesign::Pad] Pad002
  Direction = (0,1,0)
  Length = 0.9
  Length2 = 10
  Profile = -> Binder009
  Refine = true
  Suppressed = false
  Type = 0
  expr: Length = VarSet.MountingPlateThickness
FEATURE [PartDesign::Body] Body003  label="MountingPlate"
  AllowCompound = false
  Group = -> [Binder009,Pad002]
  Origin = -> Origin004
  Tip = -> Pad002
FEATURE [PartDesign::SubShapeBinder] Binder010
  BindCopyOnChange = 0
  BindMode = 0
  ClaimChildren = false
  Context = -> Part [Body007.Binder010.]
  Fuse = false
  MakeFace = true
  OffsetFill = false
  OffsetIntersection = false
  OffsetJoinType = 0
  OffsetOpenResult = false
  PartialLoad = false
  Refine = true
  Relative = true
  Support = -> [Sketch001[Edge7,Edge8,Edge9,Edge10]]
  _Version = 2
FEATURE [PartDesign::Revolution] Revolution003
  Angle = 360
  Angle2 = 60
  Axis = (1e-16,1,-1e-16)
  Base = (0,0,0)
  Profile = -> Binder010
  ReferenceAxis = -> Y_Axis008
  Refine = true
  Suppressed = false
  Type = 0
FEATURE [PartDesign::Body] Body007  label="Magnet"
  AllowCompound = false
  Group = -> [Binder010,Revolution003]
  Origin = -> Origin008
  Tip = -> Revolution003
FEATURE [Part::Part2DObjectPython] InvoluteGear  # Draft 2D object (typed FeaturePython)
  AddendumCoefficient = 1
  AttachmentSupport = -> [DatumPlane]
  DedendumCoefficient = 1.25
  ExternalGear = true
  HighPrecision = true
  MapMode = 5
  Modules = 0.16
  NumberOfTeeth = 12
  Placement = pos=(0,-9.15,0) rot=(0.57735,-0.57735,0.57735;2.0944rad)
  PressureAngle = 20
  ProfileShiftCoefficient = 0
  RootFilletCoefficient = 0.38
FEATURE [PartDesign::SubShapeBinder] Binder011
  BindCopyOnChange = 0
  BindMode = 0
  ClaimChildren = false
  Context = -> Part [Body001.Binder011.]
  Fuse = false
  MakeFace = true
  OffsetFill = false
  OffsetIntersection = false
  OffsetJoinType = 0
  OffsetOpenResult = false
  PartialLoad = false
  Refine = true
  Relative = true
  Support = -> [Body[Pad.Edge2]]
  _Version = 2
FEATURE [PartDesign::Pad] Pad003
  Direction = (0,-1,0)
  Length = 2.5
  Length2 = 10
  Placement = pos=(0,-9.15,0) rot=(0.57735,-0.57735,0.57735;2.0944rad)
  Profile = -> InvoluteGear
  ReferenceAxis = -> InvoluteGear [N_Axis]
  Refine = true
  Reversed = true
  Suppressed = false
  Type = 0
  expr: Length = VarSet.GearHeadLength
FEATURE [PartDesign::Pocket] Pocket001
  BaseFeature = -> Pad003
  Direction = (0,-1,0)
  Length = 0
  Length2 = 5
  Placement = pos=(0,-9.15,0) rot=(0.57735,-0.57735,0.57735;2.0944rad)
  Profile = -> Binder011
  Refine = true
  Suppressed = false
  Type = 3
  UpToFace = -> Pad003 [Face122]
FEATURE [PartDesign::Body] Body001  label="GearHead"
  AllowCompound = false
  Group = -> [InvoluteGear,Binder011,Pad003,Pocket001]
  Origin = -> Origin002
  Tip = -> Pocket001
FEATURE [PartDesign::Plane] DatumPlane004  label="ConnectorBodyDatum"
  AttachmentSupport = -> [Sketch,XY_Plane001]
  Length = 10
  MapMode = 6
  Placement = pos=(0,-1.1e-15,-5) rot=(0,0,1;3.14159rad)
  ResizeMode = 1
  Width = 10
FEATURE [Sketcher::SketchObject] Sketch006  label="ConnectorBodyMasterSketch"
  ArcFitTolerance = 1e-06
  AttachmentSupport = -> [DatumPlane004]
  ExternalGeometry = -> [Sketch]
  FullyConstrained = true
  MakeInternals = false
  MapMode = 5
  Placement = pos=(0,-1.1e-15,-5) rot=(0,0,1;3.14159rad)
  expr: Constraints[11] = VarSet.ConnectorBodyThickness
  expr: Constraints[33] = VarSet.ConnectorBodyLateralClearance
  expr: Constraints[34] = VarSet.ConnectorBodyForwardClearance
  expr: Constraints[38] = VarSet.PinDiameter
  expr: Constraints[45] = VarSet.PinOffset
  sketch-geometry (19):
    g0: LineSegment StartX=-2.8 StartY=-0.65 StartZ=0 EndX=2.8 EndY=-0.65 EndZ=0
    g1: LineSegment StartX=2.8 StartY=-0.65 StartZ=0 EndX=2.8 EndY=0.65 EndZ=0
    g2: LineSegment StartX=2.8 StartY=0.65 StartZ=0 EndX=-2.8 EndY=0.65 EndZ=0
    g3: LineSegment StartX=-2.8 StartY=0.65 StartZ=0 EndX=-2.8 EndY=-0.65 EndZ=0
    g4: GeomPoint [constr] X=0 Y=0 Z=0
    g5: LineSegment StartX=-2.9 StartY=0.65 StartZ=0 EndX=-2.9 EndY=-0.65 EndZ=0
    g6: LineSegment StartX=-2.4 StartY=-1.15 StartZ=0 EndX=2.4 EndY=-1.15 EndZ=0
    g7: LineSegment StartX=2.9 StartY=-0.65 StartZ=0 EndX=2.9 EndY=0.65 EndZ=0
    g8: LineSegment StartX=2.4 StartY=1.15 StartZ=0 EndX=-2.4 EndY=1.15 EndZ=0
    g9: ArcOfCircle CenterX=-2.4 CenterY=0.65 CenterZ=0 NormalX=0 NormalY=0 NormalZ=1 AngleXU=0 Radius=0.5 StartAngle=1.5708 EndAngle=3.14159
    g10: ArcOfCircle CenterX=-2.4 CenterY=-0.65 CenterZ=0 NormalX=0 NormalY=0 NormalZ=1 AngleXU=0 Radius=0.5 StartAngle=3.14159 EndAngle=4.71239
    g11: ArcOfCircle CenterX=2.4 CenterY=-0.65 CenterZ=0 NormalX=0 NormalY=0 NormalZ=1 AngleXU=0 Radius=0.5 StartAngle=4.71239 EndAngle=6.28319
    g12: ArcOfCircle CenterX=2.4 CenterY=0.65 CenterZ=0 NormalX=0 NormalY=0 NormalZ=1 AngleXU=0 Radius=0.5 StartAngle=1e-16 EndAngle=1.5708
    g13: GeomPoint [constr] X=-2.9 Y=1.15 Z=0
    g14: GeomPoint [constr] X=2.9 Y=-1.15 Z=0
    g15: Circle CenterX=-2.1 CenterY=0.15 CenterZ=0 NormalX=0 NormalY=0 NormalZ=1 AngleXU=0 Radius=0.45
    g16: Circle CenterX=-0.7 CenterY=-0.15 CenterZ=0 NormalX=0 NormalY=0 NormalZ=1 AngleXU=0 Radius=0.45
    g17: Circle CenterX=0.7 CenterY=0.15 CenterZ=0 NormalX=0 NormalY=0 NormalZ=1 AngleXU=0 Radius=0.45
    g18: Circle CenterX=2.1 CenterY=-0.15 CenterZ=0 NormalX=0 NormalY=0 NormalZ=1 AngleXU=0 Radius=0.45
  constraints (46):
    c: Coincident(g0,g1)
    c: Coincident(g1,g2)
    c: Coincident(g2,g3)
    c: Coincident(g3,g0)
    c: Horizontal(g0)
    c: Horizontal(g2)
    c: Vertical(g1)
    c: Vertical(g3)
    c: Symmetric(g2,g0,g4)
    c: Coincident(g4,g-1)
    c: PointOnObject(g-4,g1)
    c: Distance(g1,g1) = 1.3
    c: Tangent(g5,g9) = -1.5708
    c: Tangent(g5,g10) = -1.5708
    c: Tangent(g6,g10) = -1.5708
    c: Tangent(g6,g11) = -1.5708
    c: Tangent(g7,g11) = -1.5708
    c: Tangent(g7,g12) = -1.5708
    c: Tangent(g8,g12) = -1.5708
    c: Tangent(g8,g9) = -1.5708
    c: Vertical(g5)
    c: Vertical(g7)
    c: Horizontal(g6)
    c: Horizontal(g8)
    c: Equal(g9,g10)
    c: Equal(g10,g11)
    c: Equal(g11,g12)
    c: PointOnObject(g13,g5)
    c: PointOnObject(g13,g8)
    c: PointOnObject(g14,g6)
    c: PointOnObject(g14,g7)
    c: Symmetric(g6,g8,g4)
    c: Radius(g9) = 0.5
    c: Distance(g3,g5) = 0.1
    c: Distance(g2,g8) = 0.5
    c: Equal(g18,g17)
    c: Equal(g17,g16)
    c: Equal(g16,g15)
    c: Diameter(g15) = 0.9
    c: Horizontal(g15,g17)
    c: Horizontal(g16,g18)
    c: Vertical(g18,g-5)
    c: Vertical(g17,g-6)
    c: Vertical(g15,g-8)
    c: Symmetric(g17,g16,g4)
    c: Distance(g-7,g16) = 0.15
FEATURE [PartDesign::SubShapeBinder] Binder012
  BindCopyOnChange = 0
  BindMode = 0
  ClaimChildren = false
  Context = -> Part [Body008.Binder012.]
  Fuse = false
  MakeFace = true
  OffsetFill = false
  OffsetIntersection = false
  OffsetJoinType = 0
  OffsetOpenResult = false
  PartialLoad = false
  Refine = true
  Relative = true
  Support = -> [Sketch006[Edge3,Edge2,Edge1,Edge4,Edge13,Edge14,Edge15,Edge16]]
  _Version = 2
FEATURE [PartDesign::Pad] Pad004
  Direction = (0,0,1)
  Length = 4
  Length2 = 10
  Profile = -> Binder012
  Refine = true
  Suppressed = false
  Type = 0
  expr: Length = VarSet.BodyDiameter / 2
FEATURE [PartDesign::SubShapeBinder] Binder013
  BindCopyOnChange = 0
  BindMode = 0
  ClaimChildren = false
  Context = -> Part [Body008.Binder013.]
  Fuse = false
  MakeFace = true
  OffsetFill = false
  OffsetIntersection = false
  OffsetJoinType = 0
  OffsetOpenResult = false
  PartialLoad = false
  Refine = true
  Relative = true
  Support = -> [Sketch[Edge9]]
  _Version = 2
FEATURE [PartDesign::Pocket] Pocket002
  BaseFeature = -> Pad004
  Direction = (0,-1,0)
  Length = 5
  Length2 = 5
  Midplane = true
  Profile = -> Binder013
  Refine = true
  Suppressed = false
  Type = 1
FEATURE [PartDesign::Body] Body008  label="ConnectorBody"
  AllowCompound = false
  Group = -> [Binder012,Pad004,Binder013,Pocket002]
  Origin = -> Origin009
  Tip = -> Pocket002
FEATURE [PartDesign::SubShapeBinder] Binder014
  BindCopyOnChange = 0
  BindMode = 0
  ClaimChildren = false
  Context = -> Part [Body004.Binder014.]
  Fuse = false
  MakeFace = true
  OffsetFill = false
  OffsetIntersection = false
  OffsetJoinType = 0
  OffsetOpenResult = false
  PartialLoad = false
  Refine = true
  Relative = true
  Support = -> [Sketch006[Edge10,Edge11,Edge9,Edge8,Edge7,Edge6,Edge5,Edge12]]
  _Version = 2
FEATURE [PartDesign::Pocket] Pocket003
  BaseFeature = -> Draft
  Direction = (0,0,-1)
  Length = 4
  Length2 = 5
  Profile = -> Binder014
  Refine = true
  Reversed = true
  Suppressed = false
  Type = 0
  expr: Length = VarSet.BodyDiameter / 2
FEATURE [PartDesign::Body] Body004  label="CanBodyFront"
  AllowCompound = false
  Group = -> [Revolution001,Sketch005,Binder006,Pocket,PolarPattern,Draft,Binder007,Binder014,Pocket003]
  Origin = -> Origin005
  Tip = -> Pocket003
FEATURE [PartDesign::FeatureBase] Clone
  BaseFeature = -> Body004
  Suppressed = false
FEATURE [PartDesign::Body] Body005  label="CanBodyRear"
  AllowCompound = false
  Group = -> [Clone]
  Origin = -> Origin006
  Placement = pos=(0,0,0) rot=(0,0,1;3.14159rad)
  Tip = -> Clone
FEATURE [PartDesign::SubShapeBinder] Binder015
  BindCopyOnChange = 0
  BindMode = 0
  ClaimChildren = false
  Context = -> Part [Body009.Binder015.]
  Fuse = false
  MakeFace = true
  OffsetFill = false
  OffsetIntersection = false
  OffsetJoinType = 0
  OffsetOpenResult = false
  PartialLoad = false
  Refine = true
  Relative = true
  Support = -> [Sketch006[Edge16,Edge15,Edge14,Edge13]]
  _Version = 2
FEATURE [PartDesign::Pad] Pad005
  Direction = (0,0,1)
  Length = 1
  Length2 = 1
  Profile = -> Binder015
  Refine = true
  Suppressed = false
  Type = 4
  expr: Length = VarSet.ConnectorBodyHeight
  expr: Length2 = VarSet.PinLength
FEATURE [PartDesign::Fillet] Fillet
  Base = -> Pad005 [Edge2,Edge8,Edge11,Edge5]
  BaseFeature = -> Pad005
  Radius = 0.3
  Refine = true
  SupportTransform = false
  Suppressed = false
  UseAllEdges = false
FEATURE [PartDesign::Body] Body009  label="Pins"
  AllowCompound = true
  Group = -> [Binder015,Pad005,Fillet]
  Origin = -> Origin010
  Tip = -> Fillet
FEATURE [PartDesign::SubShapeBinder] Binder016
  BindCopyOnChange = 0
  BindMode = 0
  ClaimChildren = false
  Context = -> Part [Body010.Binder016.]
  Fuse = false
  MakeFace = true
  OffsetFill = false
  OffsetIntersection = false
  OffsetJoinType = 0
  OffsetOpenResult = false
  PartialLoad = false
  Refine = true
  Relative = true
  Support = -> [Sketch001[Edge57,Edge56,Edge55,Edge54,Edge53,Edge58,Edge52,Edge51]]
  _Version = 2
FEATURE [PartDesign::Revolution] Revolution004
  Angle = 360
  Angle2 = 60
  Axis = (1e-16,1,-1e-16)
  Base = (0,0,0)
  Profile = -> Binder016
  ReferenceAxis = -> Y_Axis011
  Refine = true
  Reversed = true
  Suppressed = false
  Type = 0
FEATURE [PartDesign::Body] Body010  label="CoilFront"
  AllowCompound = false
  Group = -> [Binder016,Revolution004]
  Origin = -> Origin011
  Tip = -> Revolution004
FEATURE [PartDesign::FeatureBase] Clone001
  BaseFeature = -> Body010
  Suppressed = false
FEATURE [PartDesign::Body] Body011  label="CoilRear"
  AllowCompound = false
  Group = -> [Clone001]
  Origin = -> Origin012
  Placement = pos=(0,0,0) rot=(0,0,1;3.14159rad)
  Tip = -> Clone001
FEATURE [PartDesign::SubShapeBinder] Binder017
  BindCopyOnChange = 0
  BindMode = 0
  ClaimChildren = false
  Context = -> Part [Body012.Binder017.]
  Fuse = false
  MakeFace = true
  OffsetFill = false
  OffsetIntersection = false
  OffsetJoinType = 0
  OffsetOpenResult = false
  PartialLoad = false
  Refine = true
  Relative = true
  Support = -> [Sketch001[Edge40,Edge41,Edge39,Edge31,Edge42,Edge33,Edge30,Edge34]]
  _Version = 2
FEATURE [PartDesign::Revolution] Revolution005
  Angle = 360
  Angle2 = 60
  Axis = (1e-16,1,-1e-16)
  Base = (0,0,0)
  Profile = -> Binder017
  ReferenceAxis = -> Y_Axis013
  Refine = true
  Reversed = true
  Suppressed = false
  Type = 0
FEATURE [PartDesign::ShapeBinder] ShapeBinder
  Support = -> [Sketch]
  TraceSupport = false
FEATURE [Sketcher::SketchObject] Sketch007
  ArcFitTolerance = 1e-06
  AttachmentSupport = -> [Revolution005]
  ExternalGeometry = -> [ShapeBinder]
  FullyConstrained = true
  MakeInternals = false
  MapMode = 5
  Placement = pos=(-3e-16,-2.8,3e-16) rot=(1,0,0;1.5708rad)
  sketch-geometry (5):
    g0: ArcOfCircle CenterX=0 CenterY=0 CenterZ=0 NormalX=0 NormalY=0 NormalZ=1 AngleXU=0 Radius=1.5 StartAngle=1.97773 EndAngle=2.21106
    g1: ArcOfCircle CenterX=0 CenterY=0 CenterZ=0 NormalX=0 NormalY=0 NormalZ=1 AngleXU=0 Radius=1.6 StartAngle=1.97773 EndAngle=2.21106
    g2: LineSegment StartX=-0.63327 StartY=1.46934 StartZ=0 EndX=-0.593691 EndY=1.37751 EndZ=0
    g3: LineSegment [constr] StartX=-0.955853 StartY=1.2831 StartZ=0 EndX=-0.896112 EndY=1.20291 EndZ=0
    g4: LineSegment StartX=-0.955853 StartY=1.2831 StartZ=0 EndX=-0.896112 EndY=1.20291 EndZ=0
  constraints (11):
    c: Coincident(g0,g-1)
    c: Coincident(g1,g0)
    c: Coincident(g2,g1)
    c: Coincident(g2,g0)
    c: Coincident(g0,g-3)
    c: Coincident(g1,g-6)
    c: Coincident(g3,g-5)
    c: Coincident(g3,g-4)
    c: Coincident(g4,g1)
    c: Coincident(g4,g0)
    c: Tangent(g4,g3)
FEATURE [PartDesign::Pocket] Pocket004
  BaseFeature = -> Revolution005
  Direction = (0,1,-2e-16)
  Length = 0
  Length2 = 5
  Profile = -> Sketch007
  ReferenceAxis = -> Sketch007 [N_Axis]
  Refine = true
  Suppressed = false
  Type = 3
  UpToFace = -> Revolution005 [Face6]
FEATURE [PartDesign::PolarPattern] PolarPattern001
  Angle = 360
  Axis = -> Sketch007 [N_Axis]
  BaseFeature = -> Pocket004
  Mode = 0
  Occurrences = 6
  Offset = 120
  Originals = -> [Pocket004]
  Refine = true
  Suppressed = false
  TransformMode = 0
  expr: Occurrences = VarSet.NumFingers
FEATURE [PartDesign::Draft] Draft001
  Angle = 10
  Base = -> PolarPattern001 [Face4,Face21,Face6,Face18,Face16,Face13,Face10,Face7,Face15,Face19,Face12,Face9]
  BaseFeature = -> PolarPattern001
  NeutralPlane = -> PolarPattern001 [Face30]
  Refine = true
  SupportTransform = false
  Suppressed = false
FEATURE [PartDesign::Body] Body012  label="PolePlateFront"
  AllowCompound = false
  Group = -> [Binder017,Revolution005,Sketch007,Pocket004,PolarPattern001,Draft001,ShapeBinder]
  Origin = -> Origin013
  Placement = pos=(0,0,0) rot=(0,1,0;5.75959rad)
  Tip = -> Draft001
  expr: .Placement.Rotation.Angle = 360 - 360 / VarSet.NumFingers / 2
FEATURE [PartDesign::FeatureBase] Clone002
  BaseFeature = -> Body012
  Placement = pos=(0,0,0) rot=(0,1,0;5.75959rad)
  Suppressed = false
FEATURE [PartDesign::Body] Body013  label="PolePlateRear"
  AllowCompound = false
  Group = -> [Clone002]
  Origin = -> Origin014
  Placement = pos=(0,0,0) rot=(0,0,1;3.14159rad)
  Tip = -> Clone002
FEATURE [App::Part] Part
  Group = -> [Sketch,Sketch004,Sketch006,Sketch001,VarSet,DatumPlane,DatumPlane001,DatumPlane002,DatumPlane004,DatumPlane003,Body,Body001,Body002,Body003,Body004,Body005,Body006,Body007,Body008,Body009,Body011,Body010,Body013,Body012]
  Origin = -> Origin001
  Placement = pos=(0,0,5) rot=(0,0,1;1.5708rad)
  expr: .Placement.Base.z = VarSet.BodyDiameter / 2 + VarSet.ConnectorBodyHeight
FEATURE [App::Link] Part001
  LinkPlacement = pos=(0,-5.96047e-07,5) rot=(0,0,1;1.5708rad)
  LinkedObject = -> Part
  Placement = pos=(0,-5.96047e-07,5) rot=(0,0,1;1.5708rad)
FEATURE [App::FeaturePython] GroundedJoint  # Assembly grounded joint (typed FeaturePython)
  ObjectToGround = -> Part001
  Placement = pos=(0,-5.96047e-07,5) rot=(0,0,1;0rad)
FEATURE [Assembly::JointGroup] Joints
  Group = -> [GroundedJoint]
FEATURE [Assembly::AssemblyObject] Assembly
  Group = -> [Joints,Part001,GroundedJoint]
  Origin = -> Origin015
  Type = Assembly
